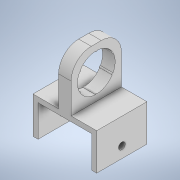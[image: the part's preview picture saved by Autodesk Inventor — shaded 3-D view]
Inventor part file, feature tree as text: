
AUTODESK INVENTOR PART (.ipt)
format: ipt  version: 2022 (Build 260153000, 153)  size: 174,592 bytes
history: native  units: mm
features: reference x6, other x5, extrude x3, sketch x3, fillet x1, projected_geometry x1
ambient origin geometry x8: Origin, YZ Plane, XZ Plane, XY Plane, X Axis, Y Axis, Z Axis, Center Point
bodies: Solid1 (feature_tree)
feature tree (19):
  extrude  "Extrusion1"  Depth=3.0mm
  extrude  "Extrusion2"  Depth=30.0mm
  extrude  "Extrusion3"  Depth=12.0mm
  fillet  "Fillet1"  Radius=30.0mm
  sketch  "Sketch2"  dims[d1=0.3mm d2=3.0mm]
  reference  "Reference9"
  reference  "Reference10"
  reference  "Reference11"
  reference  "Reference12"
  sketch  "Sketch3"  dims[d5=32.0mm d9=30.0mm]
  reference  "Reference13"
  reference  "Reference14"
  sketch  "Sketch4"  dims[d10=7.5mm d11=3.75mm d12=30.0mm d13=0.0mm d14=4.0mm d15=6.593302mm d16=60.0mm d17=0.0mm d18=0.3mm d19=3.0mm d20=22.5mm d21=1.0mm d22=60.0mm d24=360.0deg d26=10.0mm d27=0.0mm d28=12.0mm]
  projected_geometry  "Projected Loop1"
  other  "<userpath>\OneDrive\Escritorio\Mini_Proyecto_Diseno\Diseno_18012\Modelo_MPD\Carril.iam"
  other  "Carril.iam"
  other  "Base_Carril:1"
  other  "Lateral_Carril:2"
  other  "Lateral_Carril:1"
